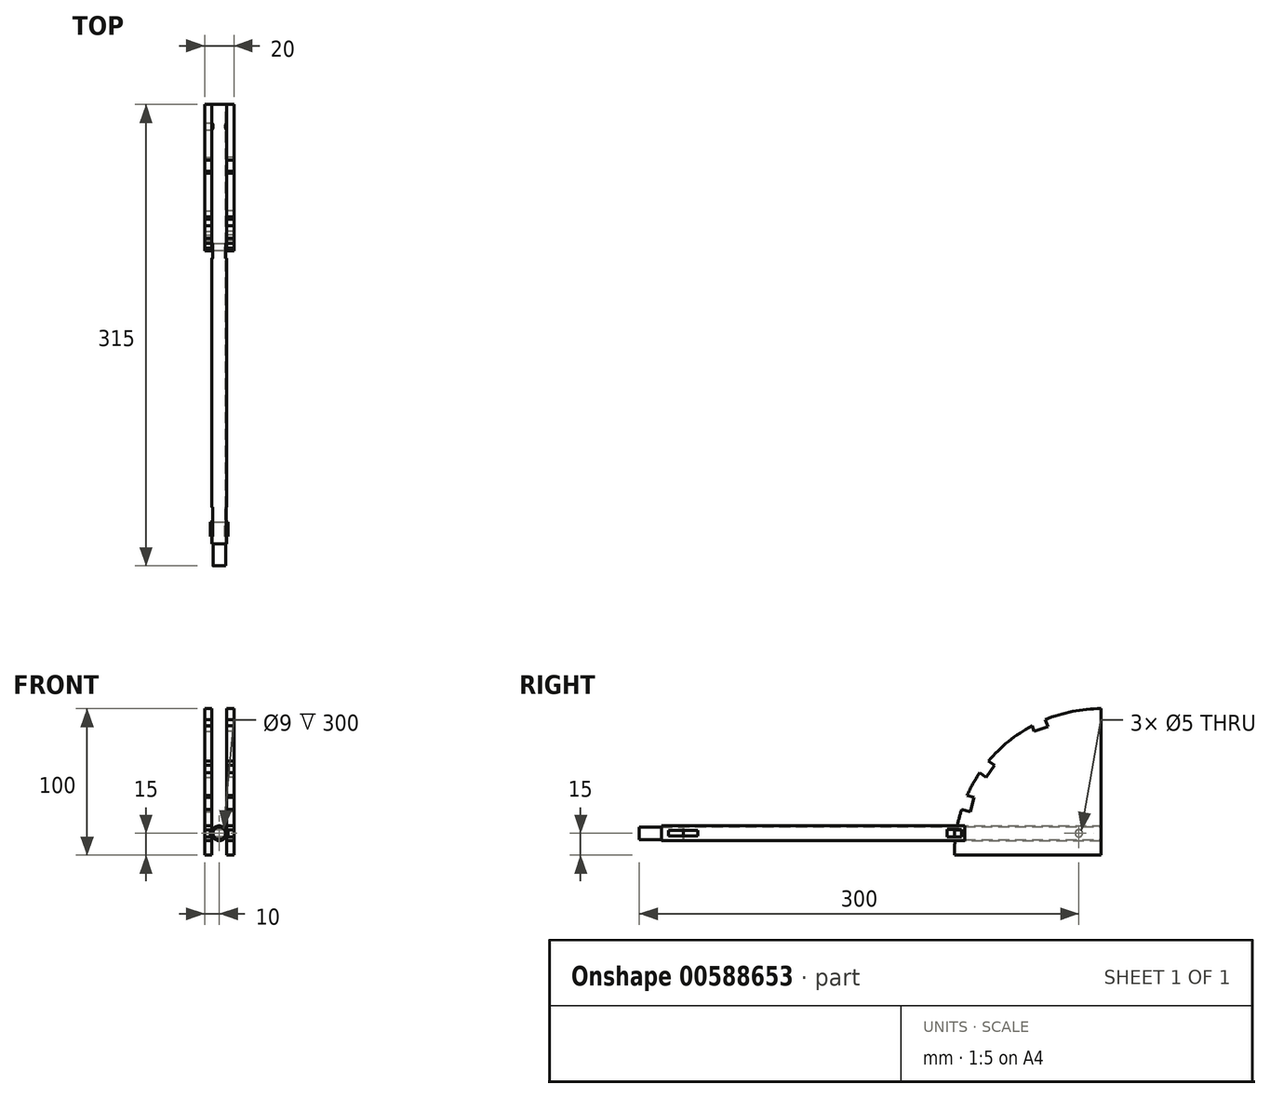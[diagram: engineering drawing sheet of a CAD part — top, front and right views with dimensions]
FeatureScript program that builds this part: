
annotation { "Feature Type Name" : "Feature", "Feature Type Description" : "" }
export const myFeature = defineFeature(function(context is Context, id is Id, definition is map)
    precondition{}
    {
        {
            var Q0;
            Q0=qCreatedBy(makeId("Right.planeOp"),FACE);
            cPlane(context, id + "F0", {"entities" : qUnion([Q0]), "cplaneType" : CPlaneType.OFFSET, "offset" : 5 * mm, "width" : 152.4 * mm, "height" : 152.4 * mm});
        }
        {
            var Q0;
            Q0=qCreatedBy(id+"F0.planeOp",FACE);
            var sketch = newSketch(context, id + "F1", { "sketchPlane" : qUnion([Q0])});
            skLineSegment(sketch, "E0", {"start": v(-85, -15) * mm, "end": v(15, -15) * mm});
            skArc(sketch, "E1", {"start": v(-85, -15) * mm, "mid": v(-84.87, -10) * mm, "end": v(-84.5, -5) * mm});
            skLineSegment(sketch, "E2", {"start": v(15, -15) * mm, "end": v(15, 85) * mm});
            skLineSegment(sketch, "E3", {"start": v(-84.5, -5) * mm, "end": v(-77.98, -5) * mm});
            skLineSegment(sketch, "E4", {"start": v(-77.98, -5) * mm, "end": v(-77.98, 5) * mm});
            skLineSegment(sketch, "E5", {"start": v(-77.98, 5) * mm, "end": v(-82.98, 5) * mm});
            skLineSegment(sketch, "E6", {"start": v(0, 0) * mm, "end": v(-78.3, 20.98) * mm, "construction": true});
            skLineSegment(sketch, "E7", {"start": v(0, 0) * mm, "end": v(-64.75, 45.34) * mm, "construction": true});
            skLineSegment(sketch, "E8", {"start": v(0, 0) * mm, "end": v(-27.49, 75.52) * mm, "construction": true});
            skLineSegment(sketch, "E9", {"start": v(-74.13, 14.69) * mm, "end": v(-71.54, 24.35) * mm});
            skLineSegment(sketch, "E10", {"start": v(-71.54, 24.35) * mm, "end": v(-76.37, 25.64) * mm});
            skLineSegment(sketch, "E11", {"start": v(-74.13, 14.69) * mm, "end": v(-79.99, 16.26) * mm});
            skLineSegment(sketch, "E12", {"start": v(-63.27, 38.2) * mm, "end": v(-57.53, 46.39) * mm});
            skLineSegment(sketch, "E13", {"start": v(-57.53, 46.39) * mm, "end": v(-61.63, 49.25) * mm});
            skLineSegment(sketch, "E14", {"start": v(-63.27, 38.2) * mm, "end": v(-67.66, 41.27) * mm});
            skLineSegment(sketch, "E15", {"start": v(-30.59, 69.42) * mm, "end": v(-21.2, 72.84) * mm});
            skLineSegment(sketch, "E16", {"start": v(-21.2, 72.84) * mm, "end": v(-22.9, 77.54) * mm});
            skLineSegment(sketch, "E17", {"start": v(-30.59, 69.42) * mm, "end": v(-31.99, 73.27) * mm});
            skArc(sketch, "E18.trimOffspring", {"start": v(-82.98, 5) * mm, "mid": v(-81.65, 10.67) * mm, "end": v(-79.99, 16.26) * mm});
            skArc(sketch, "E19.trimOffspring", {"start": v(-76.37, 25.64) * mm, "mid": v(-72.37, 33.65) * mm, "end": v(-67.66, 41.27) * mm});
            skArc(sketch, "E20.trimOffspring", {"start": v(-61.63, 49.25) * mm, "mid": v(-47.96, 62.69) * mm, "end": v(-31.99, 73.27) * mm});
            skArc(sketch, "E21.trimOffspring", {"start": v(-22.9, 77.54) * mm, "mid": v(-4.31, 83.12) * mm, "end": v(15, 85) * mm});
            skPoint(sketch, "E22", {"position": v(0, 0) * mm});
            skSolve(sketch);
        }
        {
            var Q0;
            Q0=makeQuery(id+"F1.imprint","IMPRINT",FACE,{"disambiguationData":[TD([[makeQuery(id+"F1.imprint","IMPRINT",EDGE,{"derivedFrom":sQuery(id+"F1.wireOp",EDGE,"E0")}),1.0]])]});
            extrude(context, id + "F2", {"entities" : qUnion([Q0]), "depth" : 5 * mm, "offsetDistance" : 25 * mm});
        }
        {
            var Q0;
            Q0=makeQuery(id+"F2.opExtrude","SWEPT_BODY",BODY,{"disambiguationData":[OSD([sQuery(id+"F1.wireOp",EDGE,"E0"),sQuery(id+"F1.wireOp",EDGE,"E1"),sQuery(id+"F1.wireOp",EDGE,"E2"),sQuery(id+"F1.wireOp",EDGE,"E3"),sQuery(id+"F1.wireOp",EDGE,"E4"),sQuery(id+"F1.wireOp",EDGE,"E5"),sQuery(id+"F1.wireOp",EDGE,"E9"),sQuery(id+"F1.wireOp",EDGE,"E10"),sQuery(id+"F1.wireOp",EDGE,"E11"),sQuery(id+"F1.wireOp",EDGE,"E12"),sQuery(id+"F1.wireOp",EDGE,"E13"),sQuery(id+"F1.wireOp",EDGE,"E14"),sQuery(id+"F1.wireOp",EDGE,"E15"),sQuery(id+"F1.wireOp",EDGE,"E16"),sQuery(id+"F1.wireOp",EDGE,"E17"),sQuery(id+"F1.wireOp",EDGE,"E18.trimOffspring"),sQuery(id+"F1.wireOp",EDGE,"E19.trimOffspring"),sQuery(id+"F1.wireOp",EDGE,"E20.trimOffspring"),sQuery(id+"F1.wireOp",EDGE,"E21.trimOffspring")])]});
            var Q1;
            Q1=qCreatedBy(makeId("Right.planeOp"),FACE);
            mirror(context, id + "F3", {"entities" : qUnion([Q0]), "mirrorPlane" : qUnion([Q1])});
        }
        {
            var Q0;
            Q0=qCreatedBy(makeId("Front.planeOp"),FACE);
            cPlane(context, id + "F4", {"entities" : qUnion([Q0]), "cplaneType" : CPlaneType.OFFSET, "offset" : 15 * mm, "oppositeDirection" : true, "width" : 150 * mm, "height" : 150 * mm});
        }
        {
            var Q0;
            Q0=qCreatedBy(id+"F4.planeOp",FACE);
            var sketch = newSketch(context, id + "F5", { "sketchPlane" : qUnion([Q0])});
            skCircle(sketch, "E23", {"center": v(0, 0) * mm, "radius": 5 * mm});
            skCircle(sketch, "E24", {"center": v(0, 0) * mm, "radius": 4.5 * mm});
            skSolve(sketch);
        }
        {
            var Q0;
            Q0=makeQuery(id+"F5.imprint","IMPRINT",FACE,{"disambiguationData":[TD([[makeQuery(id+"F5.imprint","IMPRINT",EDGE,{"derivedFrom":sQuery(id+"F5.wireOp",EDGE,"E23")}),1.0]])]});
            extrude(context, id + "F6", {"entities" : qUnion([Q0]), "depth" : 300 * mm, "offsetDistance" : 25 * mm});
        }
        {
            var Q0;
            Q0=qCreatedBy(id+"F0.planeOp",FACE);
            var sketch = newSketch(context, id + "F7", { "sketchPlane" : qUnion([Q0])});
            skLineSegment(sketch, "E25.bottom", {"start": v(-260, 2) * mm, "end": v(-280, 2) * mm});
            skLineSegment(sketch, "E25.top", {"start": v(-260, -2) * mm, "end": v(-280, -2) * mm});
            skLineSegment(sketch, "E25.left", {"start": v(-260, 2) * mm, "end": v(-260, -2) * mm});
            skLineSegment(sketch, "E25.right", {"start": v(-280, 2) * mm, "end": v(-280, -2) * mm});
            skSolve(sketch);
        }
        {
            var Q0;
            Q0 = qSketchRegion(id + "F7", true);
            var Q1;
            Q1=makeQuery(id+"F7.imprint","IMPRINT",FACE,{"disambiguationData":[TD([[makeQuery(id+"F7.imprint","IMPRINT",EDGE,{"derivedFrom":sQuery(id+"F7.wireOp",EDGE,"E25.bottom")}),1.0]])]});
            extrude(context, id + "F8", {"entities" : qUnion([Q0, Q1]), "operationType" : NewBodyOperationType.REMOVE, "oppositeDirection" : true, "depth" : 25 * mm, "offsetDistance" : 25 * mm});
        }
        {
            var Q0;
            Q0=makeQuery(id+"F6.opExtrude","CAP_FACE",FACE,{"disambiguationData":[OSD([sQuery(id+"F5.wireOp",EDGE,"E23"),sQuery(id+"F5.wireOp",EDGE,"E24")])],"isStart":false});
            var sketch = newSketch(context, id + "F9", { "sketchPlane" : qUnion([Q0])});
            skCircle(sketch, "E26", {"center": v(0, 0) * mm, "radius": 4.25 * mm});
            skSolve(sketch);
        }
        {
            var Q0;
            Q0 = qSketchRegion(id + "F9", true);
            extrude(context, id + "F10", {"entities" : qUnion([Q0]), "depth" : 15 * mm, "offsetDistance" : 25 * mm, "hasSecondDirection" : true, "secondDirectionOppositeDirection" : true, "secondDirectionDepth" : 15 * mm});
        }
        {
            var Q0;
            Q0=qCreatedBy(makeId("Right.planeOp"),FACE);
            var sketch = newSketch(context, id + "F11", { "sketchPlane" : qUnion([Q0])});
            skLineSegment(sketch, "E27.bottom", {"start": v(-280, 1.9) * mm, "end": v(-270, 1.9) * mm});
            skLineSegment(sketch, "E27.top", {"start": v(-280, -1.9) * mm, "end": v(-270, -1.9) * mm});
            skLineSegment(sketch, "E27.left", {"start": v(-280, 1.9) * mm, "end": v(-280, -1.9) * mm});
            skLineSegment(sketch, "E27.right", {"start": v(-270, 1.9) * mm, "end": v(-270, -1.9) * mm});
            skSolve(sketch);
        }
        {
            var Q0;
            Q0 = qSketchRegion(id + "F11", true);
            extrude(context, id + "F12", {"entities" : qUnion([Q0]), "operationType" : NewBodyOperationType.ADD, "depth" : 6 * mm, "offsetDistance" : 25 * mm, "hasSecondDirection" : true, "secondDirectionOppositeDirection" : true, "secondDirectionDepth" : 6 * mm});
        }
        {
            var Q0;
            Q0=qCreatedBy(makeId("Right.planeOp"),FACE);
            var sketch = newSketch(context, id + "F13", { "sketchPlane" : qUnion([Q0])});
            skLineSegment(sketch, "E28.bottom", {"start": v(-80, 2.5) * mm, "end": v(-90, 2.5) * mm});
            skLineSegment(sketch, "E28.top", {"start": v(-80, -2.5) * mm, "end": v(-90, -2.5) * mm});
            skLineSegment(sketch, "E28.left", {"start": v(-80, 2.5) * mm, "end": v(-80, -2.5) * mm});
            skLineSegment(sketch, "E28.right", {"start": v(-90, 2.5) * mm, "end": v(-90, -2.5) * mm});
            skPoint(sketch, "E28.middle", {"position": v(-85, 0) * mm});
            skSolve(sketch);
        }
        {
            var Q0;
            Q0 = qSketchRegion(id + "F13", true);
            extrude(context, id + "F14", {"entities" : qUnion([Q0]), "operationType" : NewBodyOperationType.REMOVE, "depth" : 25 * mm, "offsetDistance" : 25 * mm, "hasSecondDirection" : true, "secondDirectionOppositeDirection" : true, "secondDirectionDepth" : 25 * mm});
        }
        {
            var Q0;
            Q0=qCreatedBy(makeId("Right.planeOp"),FACE);
            var sketch = newSketch(context, id + "F15", { "sketchPlane" : qUnion([Q0])});
            skLineSegment(sketch, "E29.bottom", {"start": v(-80.2, 2.4) * mm, "end": v(-85, 2.4) * mm});
            skLineSegment(sketch, "E29.top", {"start": v(-80.2, -2.4) * mm, "end": v(-85, -2.4) * mm});
            skLineSegment(sketch, "E29.left", {"start": v(-80.2, 2.4) * mm, "end": v(-80.2, -2.4) * mm});
            skLineSegment(sketch, "E29.right", {"start": v(-85, 2.4) * mm, "end": v(-85, -2.4) * mm});
            skPoint(sketch, "E29.middle", {"position": v(-82.6, 0) * mm});
            skSolve(sketch);
        }
        {
            var Q0;
            Q0 = qSketchRegion(id + "F15", true);
            extrude(context, id + "F16", {"entities" : qUnion([Q0]), "depth" : 10 * mm, "offsetDistance" : 25 * mm, "hasSecondDirection" : true, "secondDirectionOppositeDirection" : true, "secondDirectionDepth" : 10 * mm});
        }
        {
            var Q0;
            Q0=sQuery(id+"F1.wireOp",VERTEX,"E22");
            var Q1;
            Q1=makeQuery(id+"F2.opExtrude","SWEPT_BODY",BODY,{"disambiguationData":[OSD([sQuery(id+"F1.wireOp",EDGE,"E0"),sQuery(id+"F1.wireOp",EDGE,"E1"),sQuery(id+"F1.wireOp",EDGE,"E2"),sQuery(id+"F1.wireOp",EDGE,"E3"),sQuery(id+"F1.wireOp",EDGE,"E4"),sQuery(id+"F1.wireOp",EDGE,"E5"),sQuery(id+"F1.wireOp",EDGE,"E9"),sQuery(id+"F1.wireOp",EDGE,"E10"),sQuery(id+"F1.wireOp",EDGE,"E11"),sQuery(id+"F1.wireOp",EDGE,"E12"),sQuery(id+"F1.wireOp",EDGE,"E13"),sQuery(id+"F1.wireOp",EDGE,"E14"),sQuery(id+"F1.wireOp",EDGE,"E15"),sQuery(id+"F1.wireOp",EDGE,"E16"),sQuery(id+"F1.wireOp",EDGE,"E17"),sQuery(id+"F1.wireOp",EDGE,"E18.trimOffspring"),sQuery(id+"F1.wireOp",EDGE,"E19.trimOffspring"),sQuery(id+"F1.wireOp",EDGE,"E20.trimOffspring"),sQuery(id+"F1.wireOp",EDGE,"E21.trimOffspring")])]});
            var Q2;
            Q2=makeQuery(id+"F6.opExtrude","SWEPT_BODY",BODY,{"disambiguationData":[OSD([sQuery(id+"F5.wireOp",EDGE,"E23"),sQuery(id+"F5.wireOp",EDGE,"E24")])]});
            var Q3;
            Q3=makeQuery(id+"F3.opPattern","COPY",BODY,{"derivedFrom":makeQuery(id+"F2.opExtrude","SWEPT_BODY",BODY,{"disambiguationData":[OSD([sQuery(id+"F1.wireOp",EDGE,"E0"),sQuery(id+"F1.wireOp",EDGE,"E1"),sQuery(id+"F1.wireOp",EDGE,"E2"),sQuery(id+"F1.wireOp",EDGE,"E3"),sQuery(id+"F1.wireOp",EDGE,"E4"),sQuery(id+"F1.wireOp",EDGE,"E5"),sQuery(id+"F1.wireOp",EDGE,"E9"),sQuery(id+"F1.wireOp",EDGE,"E10"),sQuery(id+"F1.wireOp",EDGE,"E11"),sQuery(id+"F1.wireOp",EDGE,"E12"),sQuery(id+"F1.wireOp",EDGE,"E13"),sQuery(id+"F1.wireOp",EDGE,"E14"),sQuery(id+"F1.wireOp",EDGE,"E15"),sQuery(id+"F1.wireOp",EDGE,"E16"),sQuery(id+"F1.wireOp",EDGE,"E17"),sQuery(id+"F1.wireOp",EDGE,"E18.trimOffspring"),sQuery(id+"F1.wireOp",EDGE,"E19.trimOffspring"),sQuery(id+"F1.wireOp",EDGE,"E20.trimOffspring"),sQuery(id+"F1.wireOp",EDGE,"E21.trimOffspring")])]}),"instanceName":"1"});
            hole(context, id + "F17", {"style" : HoleStyle.SIMPLE, "endStyle" : HoleEndStyle.THROUGH, "holeDiameter" : 5 * mm, "majorDiameter" : 5 * mm, "isTappedThrough" : true, "tappedDepth" : 12 * mm, "tapClearance" : 3, "locations" : qUnion([Q0]), "scope" : qUnion([Q1, Q2, Q3])});
        }
    });
